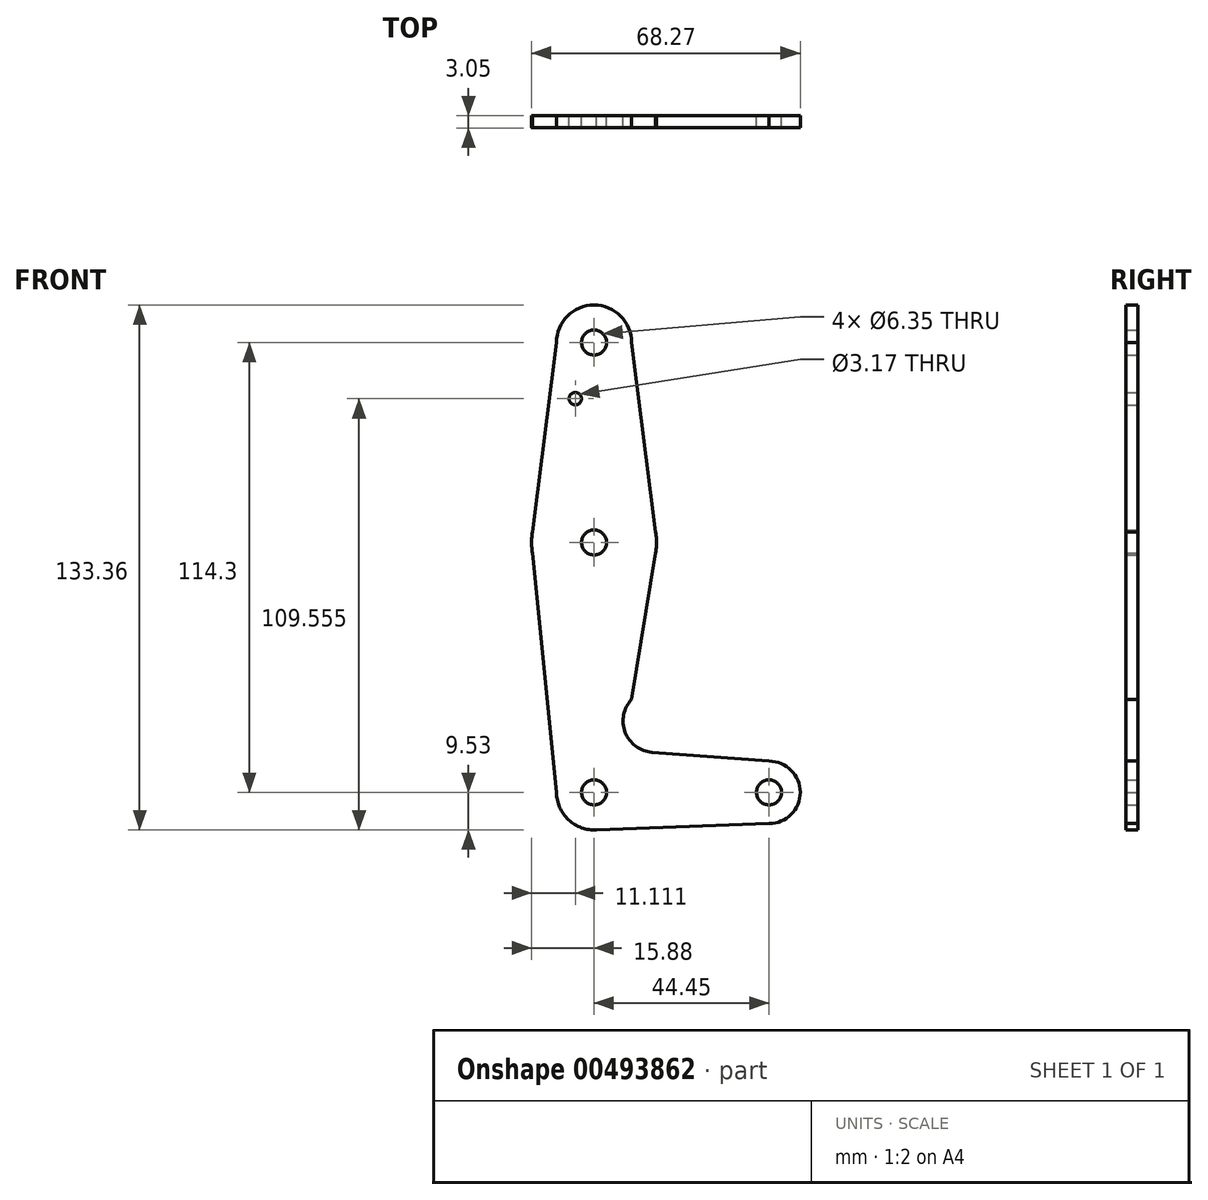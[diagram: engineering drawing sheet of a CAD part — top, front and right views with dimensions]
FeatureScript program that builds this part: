
annotation { "Feature Type Name" : "Feature", "Feature Type Description" : "" }
export const myFeature = defineFeature(function(context is Context, id is Id, definition is map)
    precondition{}
    {
        {
            var Q0;
            Q0=qCreatedBy(makeId("Front.planeOp"),FACE);
            var sketch = newSketch(context, id + "F0", { "sketchPlane" : qUnion([Q0])});
            skCircle(sketch, "E0", {"center": v(0, 114.3) * mm, "radius": 9.53 * mm});
            skCircle(sketch, "E1", {"center": v(0, 63.5) * mm, "radius": 15.88 * mm});
            skCircle(sketch, "E2", {"center": v(0, 0) * mm, "radius": 9.53 * mm});
            skCircle(sketch, "E3", {"center": v(-4.77, 100.03) * mm, "radius": 1.59 * mm});
            skCircle(sketch, "E4", {"center": v(44.45, 0) * mm, "radius": 7.94 * mm});
            skLineSegment(sketch, "E5", {"start": v(0, -9.52) * mm, "end": v(44.45, -7.94) * mm});
            skLineSegment(sketch, "E6", {"start": v(44.45, 7.94) * mm, "end": v(14.71, 10.2) * mm});
            skLineSegment(sketch, "E7", {"start": v(0, 114.3) * mm, "end": v(0, 0) * mm, "construction": true});
            skLineSegment(sketch, "E8", {"start": v(44.45, 0) * mm, "end": v(0, 0) * mm, "construction": true});
            skLineSegment(sketch, "E9", {"start": v(-15.65, 60.85) * mm, "end": v(-9.53, 0) * mm});
            skLineSegment(sketch, "E10", {"start": v(-9.53, 114.3) * mm, "end": v(-15.65, 66.15) * mm});
            skLineSegment(sketch, "E11", {"start": v(9.53, 114.3) * mm, "end": v(15.65, 66.15) * mm});
            skLineSegment(sketch, "E12", {"start": v(9.56, 23.62) * mm, "end": v(15.65, 60.85) * mm});
            skArc(sketch, "E13", {"start": v(9.56, 23.62) * mm, "mid": v(7.9, 15.28) * mm, "end": v(14.71, 10.2) * mm});
            skCircle(sketch, "E14", {"center": v(0, 114.3) * mm, "radius": 3.18 * mm});
            skCircle(sketch, "E15", {"center": v(0, 63.5) * mm, "radius": 3.18 * mm});
            skCircle(sketch, "E16", {"center": v(0, 0) * mm, "radius": 3.18 * mm});
            skCircle(sketch, "E17", {"center": v(44.45, 0) * mm, "radius": 3.18 * mm});
            skSolve(sketch);
        }
        {
            var Q0;
            Q0 = qSketchRegion(id + "F0", true);
            extrude(context, id + "F1", {"entities" : qUnion([Q0]), "depth" : 3.05 * mm, "offsetDistance" : 25.4 * mm});
        }
        {
            var Q0;
            Q0 = qSketchRegion(id + "F0", true);
            extrude(context, id + "F2", {"entities" : qUnion([Q0]), "operationType" : NewBodyOperationType.ADD, "depth" : 3.05 * mm, "offsetDistance" : 25.4 * mm});
        }
    });
